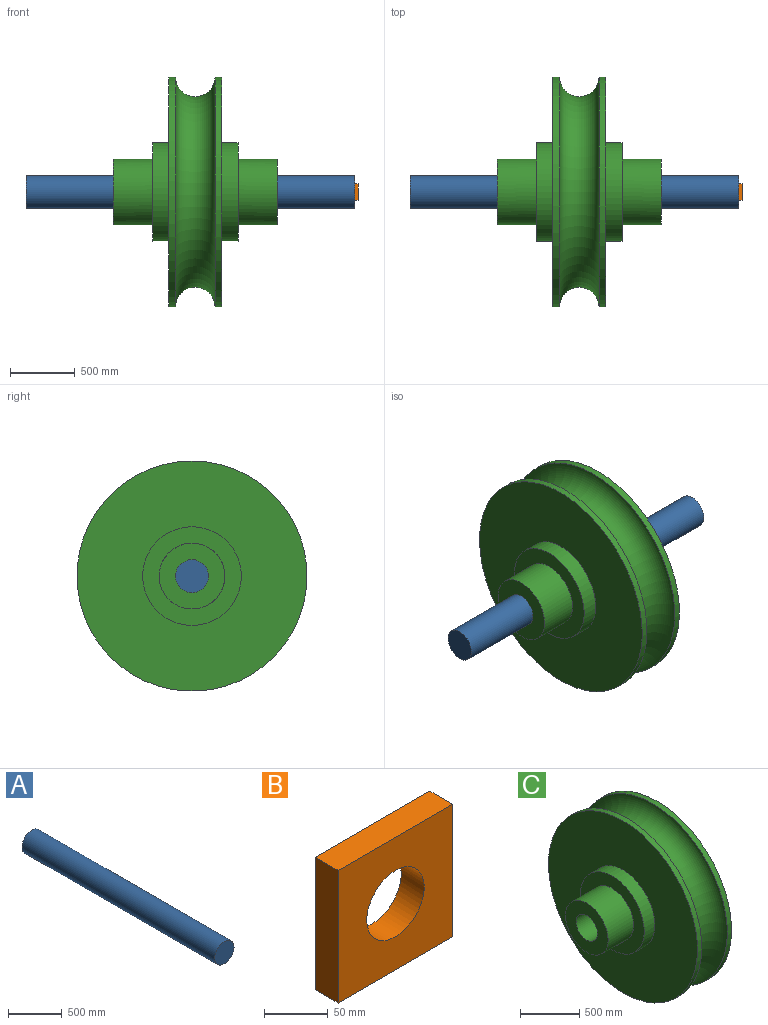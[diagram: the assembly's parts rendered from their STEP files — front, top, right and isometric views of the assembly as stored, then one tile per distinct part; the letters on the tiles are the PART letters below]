
ASSEMBLY  parts=3 mates=2
PART A: 3 faces, bbox 254x2540x254 mm
  f0: cylinder r=127mm len=2540mm, axis (0,1,0), area 2026829.9mm2, adj f1,f2
  f1: plane 254x254mm, normal (0,-1,0), area 50670.7mm2, adj f0
  f2: plane 254x254mm, normal (0,1,0), area 50670.7mm2, adj f0
PART B: 7 faces, bbox 127x25.4x127 mm
  f0: plane 127x25.4mm, normal (0,0,-1), area 3225.8mm2, adj f1,f3,f4,f5
  f1: plane 127x25.4mm, normal (1,0,0), area 3225.8mm2, adj f0,f2,f4,f5
  f2: plane 127x25.4mm, normal (0,0,1), area 3225.8mm2, adj f1,f3,f4,f5
  f3: plane 127x25.4mm, normal (-1,0,0), area 3225.8mm2, adj f0,f2,f4,f5
  f4: plane 127x127mm, normal (0,-1,0), area 12962.1mm2, adj f0,f1,f2,f3,f6
  f5: plane 127x127mm, normal (0,1,0), area 12962.1mm2, adj f0,f1,f2,f3,f6
  f6: cylinder r=31.75mm len=63.5mm, axis (0,-1,0), area 5067.1mm2, adj f4,f5
PART C: 14 faces, bbox 1270x2158.7x2158.7 mm
  f0: plane 1778x1778mm, normal (-1,0,0), area 2026829.9mm2, adj f1,f8
  f1: cylinder r=381mm len=762mm, axis (-1,0,0), area 304024.5mm2, adj f0,f2
  f2: plane 762x762mm, normal (-1,0,0), area 253353.7mm2, adj f1,f10
  f3: plane 762x762mm, normal (1,0,0), area 253353.7mm2, adj f4,f11
  f4: cylinder r=381mm len=762mm, axis (-1,0,0), area 304024.5mm2, adj f3,f5
  f5: plane 1778x1778mm, normal (1,0,0), area 2026829.9mm2, adj f4,f6
  f6: cylinder r=889mm len=1778mm, axis (-1,0,0), area 283756.2mm2, adj f5,f7
  f7: torus R=889mm, axis (-1,0,0), area 2382475.6mm2, adj f6,f8
  f8: cylinder r=889mm len=1778mm, axis (-1,0,0), area 283756.2mm2, adj f0,f7
  f9: plane 508x508mm, normal (-1,0,0), area 152012.2mm2, adj f10,f13
  f10: cylinder r=254mm len=508mm, axis (1,0,0), area 486439.2mm2, adj f2,f9
  f11: cylinder r=254mm len=508mm, axis (1,0,0), area 486439.2mm2, adj f3,f12
  f12: plane 508x508mm, normal (1,0,0), area 152012.2mm2, adj f11,f13
  f13: cylinder r=127mm len=1270mm, axis (1,0,0), area 1013415mm2, adj f9,f12
PLACE A rot(axis=(-0.58,0.58,0.58),120deg) t=(152.54,303.91,-226.17)mm
PLACE B rot(axis=(0.71,-0.71,0),180deg) t=(1435.24,303.91,-226.17)mm
PLACE C t=(190.58,303.91,-226.17)mm fixed
MATE fastened B.f6 <-> A.f0  axis (-1,0,0) through (1422.54,303.91,-226.17)mm
MATE slider A.f0 <-> C.f1  axis (-1,0,0) through (1422.54,303.91,-226.17)mm
